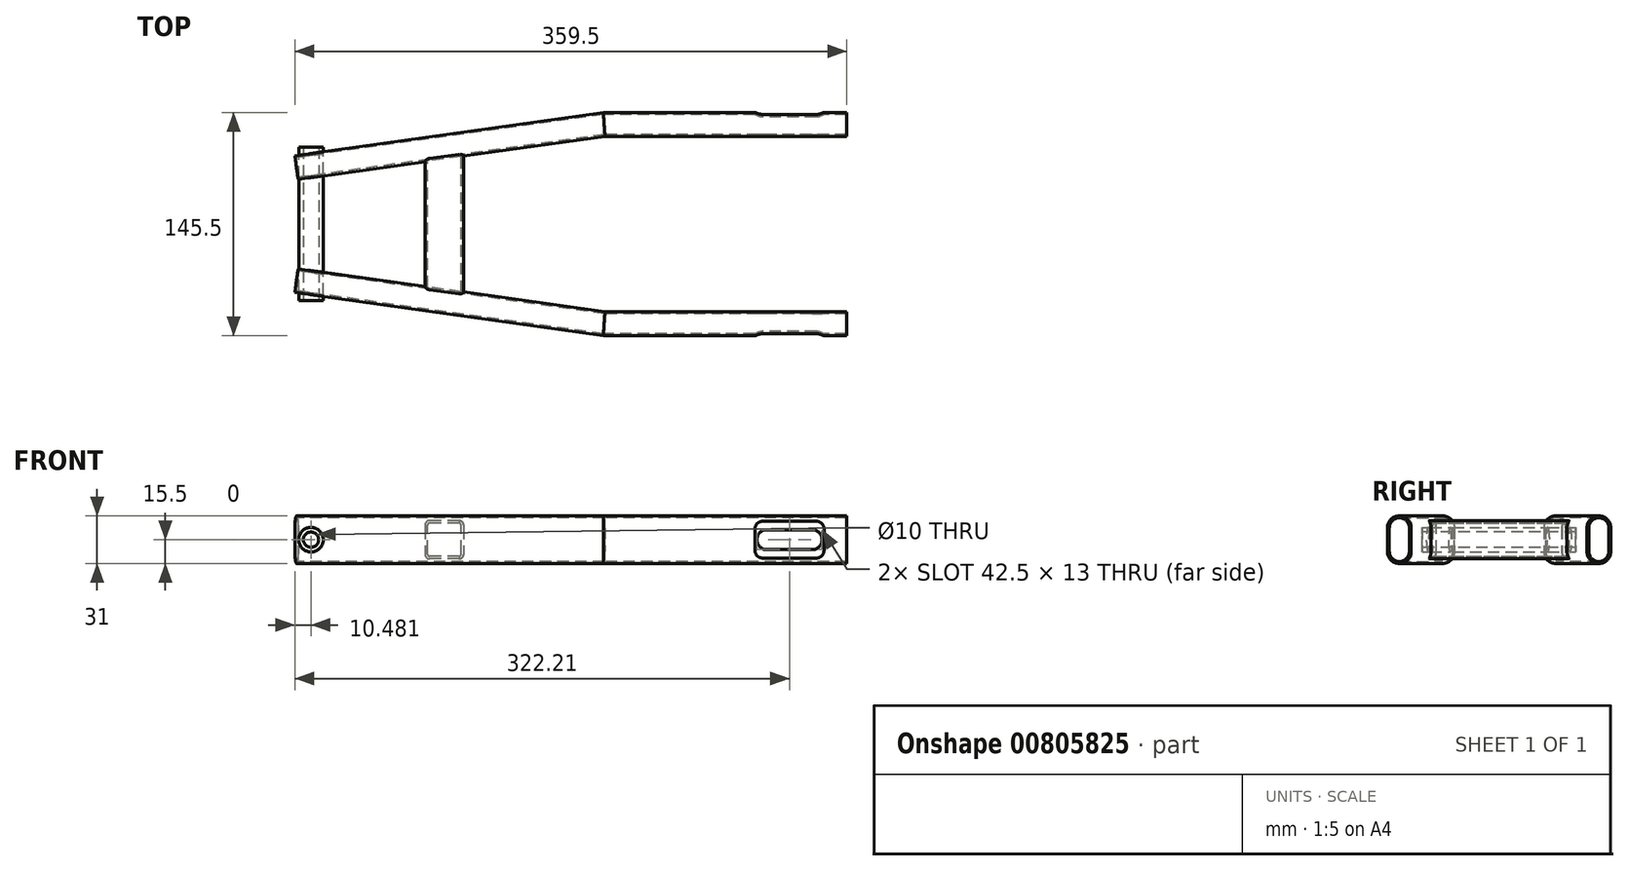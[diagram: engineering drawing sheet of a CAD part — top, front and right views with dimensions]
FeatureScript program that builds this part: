
annotation { "Feature Type Name" : "Feature", "Feature Type Description" : "" }
export const myFeature = defineFeature(function(context is Context, id is Id, definition is map)
    precondition{}
    {
        {
            var Q0;
            Q0=qCreatedBy(makeId("Top.planeOp"),FACE);
            var sketch = newSketch(context, id + "F0", { "sketchPlane" : qUnion([Q0])});
            skLineSegment(sketch, "E0", {"start": v(0, 65) * mm, "end": v(-158.03, 65) * mm});
            skLineSegment(sketch, "E1", {"start": v(-158.03, 65) * mm, "end": v(-358.42, 36.84) * mm});
            skSolve(sketch);
        }
        {
            var Q0;
            Q0=qCreatedBy(makeId("Right.planeOp"),FACE);
            var sketch = newSketch(context, id + "F1", { "sketchPlane" : qUnion([Q0])});
            skLineSegment(sketch, "E2.bottom", {"start": v(57.25, 7.75) * mm, "end": v(72.75, 7.75) * mm});
            skLineSegment(sketch, "E2.top", {"start": v(57.25, -7.75) * mm, "end": v(72.75, -7.75) * mm});
            skLineSegment(sketch, "E2.left", {"start": v(57.25, 7.75) * mm, "end": v(57.25, -7.75) * mm});
            skLineSegment(sketch, "E2.right", {"start": v(72.75, 7.75) * mm, "end": v(72.75, -7.75) * mm});
            skPoint(sketch, "E2.middle", {"position": v(65, 0) * mm});
            skArc(sketch, "E3", {"start": v(57.25, 7.75) * mm, "mid": v(65, 15.5) * mm, "end": v(72.75, 7.75) * mm});
            skArc(sketch, "E4", {"start": v(72.75, -7.75) * mm, "mid": v(65, -15.5) * mm, "end": v(57.25, -7.75) * mm});
            skArc(sketch, "E5.0", {"start": v(58.45, 7.75) * mm, "mid": v(65, 14.3) * mm, "end": v(71.55, 7.75) * mm});
            skLineSegment(sketch, "E6.0", {"start": v(58.45, 7.75) * mm, "end": v(58.45, -7.75) * mm});
            skLineSegment(sketch, "E7.0", {"start": v(71.55, 7.75) * mm, "end": v(71.55, -7.75) * mm});
            skArc(sketch, "E8.0", {"start": v(71.55, -7.75) * mm, "mid": v(65, -14.3) * mm, "end": v(58.45, -7.75) * mm});
            skSolve(sketch);
        }
        {
            var Q0;
            Q0 = qSketchRegion(id + "F1", true);
            var Q1;
            Q1 = qConstructionFilter(qBodyType(qCreatedBy(id + "F0" ,EDGE), BodyType.WIRE), ConstructionObject.NO);
            sweep(context, id + "F2", {"profiles" : qUnion([Q0]), "path" : qUnion([Q1])});
        }
        {
            var Q0;
            Q0=makeQuery(id+"F2.opSweep","SWEPT_FACE",FACE,{"disambiguationData":[OSD([sQuery(id+"F0.wireOp",EDGE,"E0"),sQuery(id+"F1.wireOp",EDGE,"E2.left")])]});
            var sketch = newSketch(context, id + "F3", { "sketchPlane" : qUnion([Q0])});
            skLineSegment(sketch, "E9.bottom", {"start": v(-52.04, 6.5) * mm, "end": v(-22.54, 6.5) * mm});
            skLineSegment(sketch, "E9.top", {"start": v(-52.04, -6.5) * mm, "end": v(-22.54, -6.5) * mm});
            skPoint(sketch, "E9.middle", {"position": v(-37.3, 0) * mm});
            skArc(sketch, "E10", {"start": v(-52.04, -6.5) * mm, "mid": v(-58.54, 0) * mm, "end": v(-52.04, 6.5) * mm});
            skArc(sketch, "E11", {"start": v(-22.54, 6.5) * mm, "mid": v(-16.04, 0) * mm, "end": v(-22.54, -6.5) * mm});
            skSolve(sketch);
        }
        {
            var Q0;
            Q0=makeQuery(id+"F3.imprint","IMPRINT",FACE,{"disambiguationData":[TD([[makeQuery(id+"F3.imprint","IMPRINT",EDGE,{"derivedFrom":sQuery(id+"F3.wireOp",EDGE,"E9.bottom")}),-1.0]])]});
            extrude(context, id + "F4", {"entities" : qUnion([Q0]), "operationType" : NewBodyOperationType.REMOVE, "oppositeDirection" : true, "depth" : 4 * mm, "offsetDistance" : 25 * mm});
        }
        {
            var Q0;
            Q0=makeQuery(id+"F2.opSweep","SWEPT_FACE",FACE,{"disambiguationData":[OSD([sQuery(id+"F0.wireOp",EDGE,"E0"),sQuery(id+"F1.wireOp",EDGE,"E2.right")])]});
            var sketch = newSketch(context, id + "F5", { "sketchPlane" : qUnion([Q0])});
            skLineSegment(sketch, "E12.bottom", {"start": v(54.76, 12) * mm, "end": v(19.76, 12) * mm});
            skLineSegment(sketch, "E12.top", {"start": v(54.76, -12) * mm, "end": v(19.76, -12) * mm});
            skLineSegment(sketch, "E12.left", {"start": v(59.76, 7) * mm, "end": v(59.76, -7) * mm});
            skLineSegment(sketch, "E12.right", {"start": v(14.76, 7) * mm, "end": v(14.76, -7) * mm});
            skPoint(sketch, "E12.middle", {"position": v(37.26, 0) * mm});
            skPoint(sketch, "E13.visualSharp", {"position": v(14.76, 12) * mm});
            skArc(sketch, "E13.filletArc", {"start": v(19.76, 12) * mm, "mid": v(16.22, 10.54) * mm, "end": v(14.76, 7) * mm});
            skPoint(sketch, "E14.visualSharp", {"position": v(59.76, 12) * mm});
            skArc(sketch, "E14.filletArc", {"start": v(59.76, 7) * mm, "mid": v(58.3, 10.54) * mm, "end": v(54.76, 12) * mm});
            skPoint(sketch, "E15.visualSharp", {"position": v(59.76, -12) * mm});
            skArc(sketch, "E15.filletArc", {"start": v(54.76, -12) * mm, "mid": v(58.3, -10.54) * mm, "end": v(59.76, -7) * mm});
            skPoint(sketch, "E16.visualSharp", {"position": v(14.76, -12) * mm});
            skArc(sketch, "E16.filletArc", {"start": v(14.76, -7) * mm, "mid": v(16.22, -10.54) * mm, "end": v(19.76, -12) * mm});
            skSolve(sketch);
        }
        {
            var Q0;
            Q0 = qSketchRegion(id + "F5", true);
            extrude(context, id + "F6", {"entities" : qUnion([Q0]), "operationType" : NewBodyOperationType.REMOVE, "oppositeDirection" : true, "depth" : 4 * mm, "offsetDistance" : 25 * mm});
        }
        {
            var Q0;
            Q0=makeQuery(id+"F2.opSweep","SWEPT_BODY",BODY,{"disambiguationData":[OSD([sQuery(id+"F0.wireOp",EDGE,"E1"),sQuery(id+"F1.wireOp",EDGE,"E2.left"),sQuery(id+"F1.wireOp",EDGE,"E2.right"),sQuery(id+"F1.wireOp",EDGE,"E3"),sQuery(id+"F1.wireOp",EDGE,"E4"),sQuery(id+"F1.wireOp",EDGE,"E5.0"),sQuery(id+"F1.wireOp",EDGE,"E6.0"),sQuery(id+"F1.wireOp",EDGE,"E7.0"),sQuery(id+"F1.wireOp",EDGE,"E8.0")])]});
            var Q1;
            Q1=qCreatedBy(makeId("Front.planeOp"),FACE);
            mirror(context, id + "F7", {"entities" : qUnion([Q0]), "mirrorPlane" : qUnion([Q1])});
        }
        {
            var Q0;
            Q0=qCreatedBy(makeId("Front.planeOp"),FACE);
            var sketch = newSketch(context, id + "F8", { "sketchPlane" : qUnion([Q0])});
            skCircle(sketch, "E17", {"center": v(-349.02, 0) * mm, "radius": 8 * mm});
            skSolve(sketch);
        }
        {
            var Q0;
            Q0 = qSketchRegion(id + "F8", true);
            extrude(context, id + "F9", {"entities" : qUnion([Q0]), "operationType" : NewBodyOperationType.ADD, "endBound" : BoundingType.SYMMETRIC, "depth" : 100 * mm, "offsetDistance" : 25 * mm});
        }
        {
            var Q0;
            Q0=makeQuery(id+"F9.opExtrude","CAP_FACE",FACE,{"disambiguationData":[OSD([sQuery(id+"F8.wireOp",EDGE,"E17")])],"isStart":false});
            var sketch = newSketch(context, id + "F10", { "sketchPlane" : qUnion([Q0])});
            skCircle(sketch, "E18", {"center": v(-349.02, 0) * mm, "radius": 5 * mm});
            skSolve(sketch);
        }
        {
            var Q0;
            Q0 = qSketchRegion(id + "F10", true);
            extrude(context, id + "F11", {"entities" : qUnion([Q0]), "operationType" : NewBodyOperationType.REMOVE, "endBound" : BoundingType.THROUGH_ALL, "oppositeDirection" : true, "depth" : 25 * mm, "offsetDistance" : 25 * mm});
        }
        {
            var Q0;
            Q0=qCreatedBy(makeId("Front.planeOp"),FACE);
            var sketch = newSketch(context, id + "F12", { "sketchPlane" : qUnion([Q0])});
            skLineSegment(sketch, "E19.bottom", {"start": v(-271.69, 12.5) * mm, "end": v(-252.69, 12.5) * mm});
            skLineSegment(sketch, "E19.top", {"start": v(-271.69, -12.5) * mm, "end": v(-252.69, -12.5) * mm});
            skLineSegment(sketch, "E19.left", {"start": v(-274.69, 9.5) * mm, "end": v(-274.69, -9.5) * mm});
            skLineSegment(sketch, "E19.right", {"start": v(-249.69, 9.5) * mm, "end": v(-249.69, -9.5) * mm});
            skPoint(sketch, "E19.middle", {"position": v(-262.19, 0) * mm});
            skPoint(sketch, "E20.visualSharp", {"position": v(-274.69, 12.5) * mm});
            skArc(sketch, "E20.filletArc", {"start": v(-271.69, 12.5) * mm, "mid": v(-273.81, 11.62) * mm, "end": v(-274.69, 9.5) * mm});
            skPoint(sketch, "E21.visualSharp", {"position": v(-249.69, 12.5) * mm});
            skArc(sketch, "E21.filletArc", {"start": v(-249.69, 9.5) * mm, "mid": v(-250.57, 11.62) * mm, "end": v(-252.69, 12.5) * mm});
            skPoint(sketch, "E22.visualSharp", {"position": v(-249.69, -12.5) * mm});
            skArc(sketch, "E22.filletArc", {"start": v(-252.69, -12.5) * mm, "mid": v(-250.57, -11.62) * mm, "end": v(-249.69, -9.5) * mm});
            skPoint(sketch, "E23.visualSharp", {"position": v(-274.69, -12.5) * mm});
            skArc(sketch, "E23.filletArc", {"start": v(-274.69, -9.5) * mm, "mid": v(-273.81, -11.62) * mm, "end": v(-271.69, -12.5) * mm});
            skLineSegment(sketch, "E24.0", {"start": v(-271.69, 10.9) * mm, "end": v(-252.69, 10.9) * mm});
            skLineSegment(sketch, "E25.0", {"start": v(-251.29, 9.5) * mm, "end": v(-251.29, -9.5) * mm});
            skLineSegment(sketch, "E26.0", {"start": v(-271.69, -10.9) * mm, "end": v(-252.69, -10.9) * mm});
            skLineSegment(sketch, "E27.0", {"start": v(-273.09, 9.5) * mm, "end": v(-273.09, -9.5) * mm});
            skArc(sketch, "E28.filletArc", {"start": v(-271.69, 10.9) * mm, "mid": v(-272.68, 10.49) * mm, "end": v(-273.09, 9.5) * mm});
            skArc(sketch, "E29.filletArc", {"start": v(-251.29, 9.5) * mm, "mid": v(-251.7, 10.49) * mm, "end": v(-252.69, 10.9) * mm});
            skArc(sketch, "E30.filletArc", {"start": v(-252.69, -10.9) * mm, "mid": v(-251.7, -10.49) * mm, "end": v(-251.29, -9.5) * mm});
            skArc(sketch, "E31.filletArc", {"start": v(-273.09, -9.5) * mm, "mid": v(-272.68, -10.49) * mm, "end": v(-271.69, -10.9) * mm});
            skSolve(sketch);
        }
        {
            var Q0;
            Q0 = qSketchRegion(id + "F12", true);
            extrude(context, id + "F13", {"entities" : qUnion([Q0]), "operationType" : NewBodyOperationType.ADD, "endBound" : BoundingType.UP_TO_NEXT, "depth" : 25 * mm, "offsetDistance" : 25 * mm, "hasSecondDirection" : true, "secondDirectionBound" : SecondDirectionBoundingType.UP_TO_NEXT, "secondDirectionOppositeDirection" : true, "secondDirectionDepth" : 25 * mm});
        }
    });
